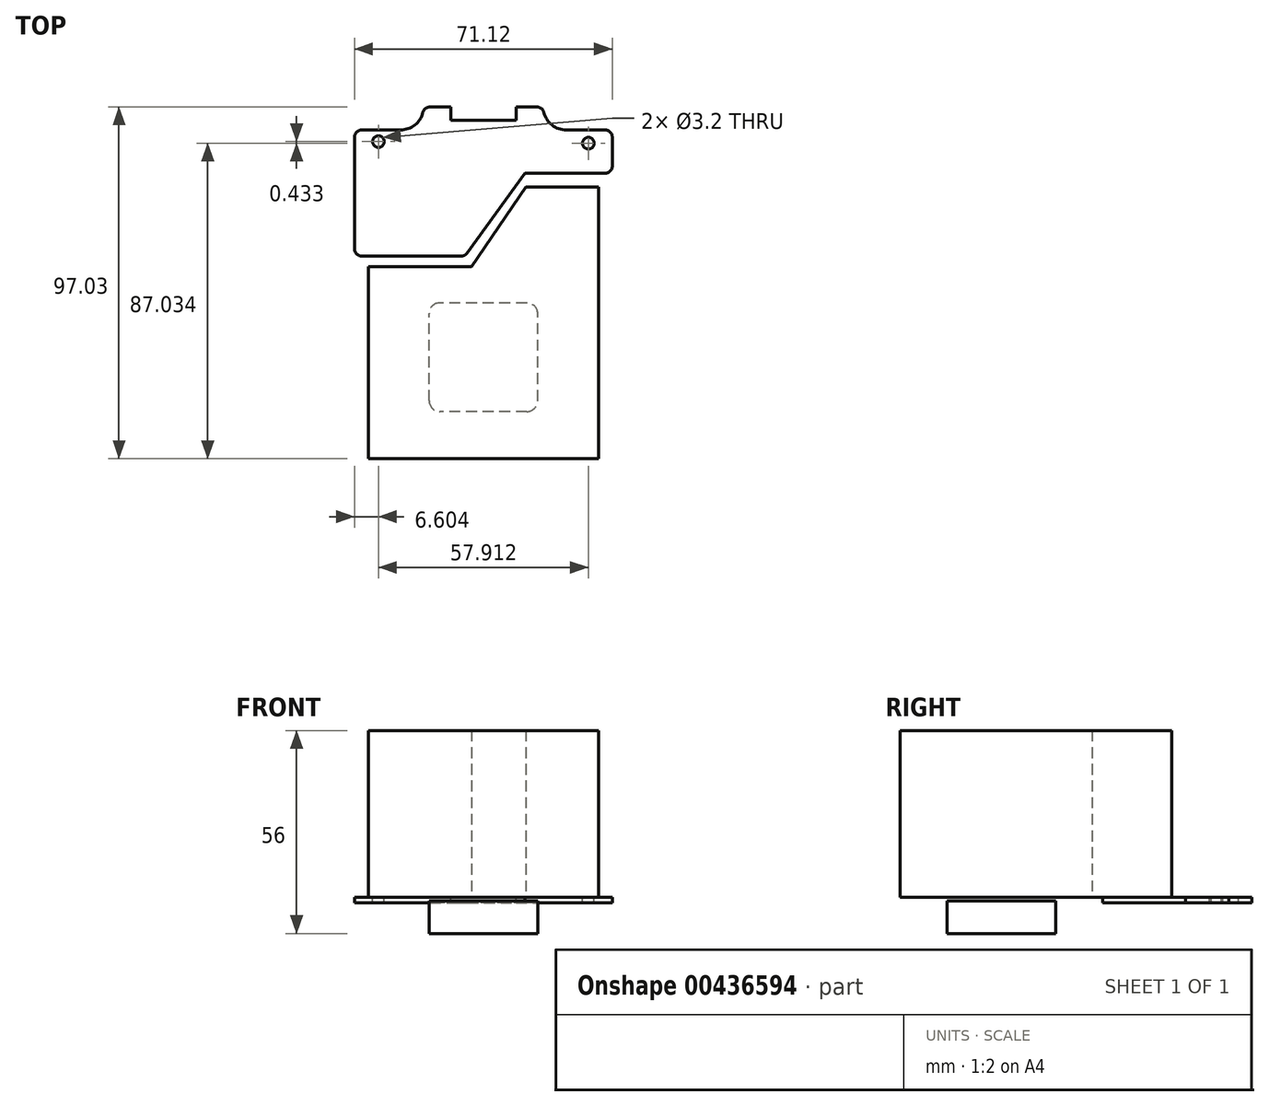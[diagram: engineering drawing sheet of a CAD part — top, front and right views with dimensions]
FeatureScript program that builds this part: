
annotation { "Feature Type Name" : "Feature", "Feature Type Description" : "" }
export const myFeature = defineFeature(function(context is Context, id is Id, definition is map)
    precondition{}
    {
        {
            var Q0;
            Q0=qCreatedBy(makeId("Top.planeOp"),FACE);
            var sketch = newSketch(context, id + "F0", { "sketchPlane" : qUnion([Q0])});
            skLineSegment(sketch, "E0.bottom", {"start": v(35.56, -55.5) * mm, "end": v(-35.56, -55.5) * mm});
            skLineSegment(sketch, "E0.top", {"start": v(35.56, 55.5) * mm, "end": v(-35.56, 55.5) * mm});
            skLineSegment(sketch, "E0.left", {"start": v(35.56, -55.5) * mm, "end": v(35.56, 55.5) * mm});
            skLineSegment(sketch, "E0.right", {"start": v(-35.56, -55.5) * mm, "end": v(-35.56, 55.5) * mm});
            skPoint(sketch, "E0.middle", {"position": v(0, 0) * mm});
            skCircle(sketch, "E1", {"center": v(-28.96, 42.13) * mm, "radius": 1.6 * mm});
            skCircle(sketch, "E2", {"center": v(28.96, 41.7) * mm, "radius": 1.6 * mm});
            skLineSegment(sketch, "E3", {"start": v(-75.95, 0) * mm, "end": v(69.97, 0) * mm, "construction": true});
            skLineSegment(sketch, "E4", {"start": v(0, -74.25) * mm, "end": v(0, 72.53) * mm, "construction": true});
            skLineSegment(sketch, "E5", {"start": v(-28.96, 42.13) * mm, "end": v(28.96, 41.7) * mm, "construction": true});
            skPoint(sketch, "E6", {"position": v(0, 41.91) * mm});
            skCircle(sketch, "E7.MirrorC", {"center": v(-28.96, -42.13) * mm, "radius": 1.6 * mm});
            skCircle(sketch, "E8.MirrorC", {"center": v(28.96, -41.7) * mm, "radius": 1.6 * mm});
            skLineSegment(sketch, "E9.bottom", {"start": v(35.56, 55.5) * mm, "end": v(16.5, 55.5) * mm});
            skLineSegment(sketch, "E9.top", {"start": v(35.56, 45.34) * mm, "end": v(22.86, 45.34) * mm});
            skLineSegment(sketch, "E9.left", {"start": v(35.56, 55.5) * mm, "end": v(35.56, 45.34) * mm});
            skLineSegment(sketch, "E9.right", {"start": v(16.5, 55.5) * mm, "end": v(16.5, 51.69) * mm});
            skPoint(sketch, "E10.visualSharp", {"position": v(16.5, 45.34) * mm});
            skArc(sketch, "E10.filletArc", {"start": v(16.5, 51.69) * mm, "mid": v(18.37, 47.2) * mm, "end": v(22.86, 45.34) * mm});
            skLineSegment(sketch, "E11.MirrorCS", {"start": v(-35.56, 45.34) * mm, "end": v(-22.86, 45.34) * mm});
            skPoint(sketch, "E12.MirrorP", {"position": v(-16.5, 45.34) * mm});
            skArc(sketch, "E13.MirrorCS", {"start": v(-16.5, 51.69) * mm, "mid": v(-18.37, 47.2) * mm, "end": v(-22.86, 45.34) * mm});
            skLineSegment(sketch, "E14.MirrorCS", {"start": v(-16.5, 55.5) * mm, "end": v(-16.5, 51.69) * mm});
            skLineSegment(sketch, "E15.MirrorCS", {"start": v(35.56, -45.34) * mm, "end": v(22.86, -45.34) * mm});
            skArc(sketch, "E16.MirrorCS", {"start": v(16.5, -51.69) * mm, "mid": v(18.37, -47.2) * mm, "end": v(22.86, -45.34) * mm});
            skLineSegment(sketch, "E17.MirrorCS", {"start": v(16.5, -55.5) * mm, "end": v(16.5, -51.69) * mm});
            skLineSegment(sketch, "E18.MirrorCS", {"start": v(-16.5, -55.5) * mm, "end": v(-16.5, -51.69) * mm});
            skArc(sketch, "E19.MirrorCS", {"start": v(-16.5, -51.69) * mm, "mid": v(-18.37, -47.2) * mm, "end": v(-22.86, -45.34) * mm});
            skLineSegment(sketch, "E20.MirrorCS", {"start": v(-35.56, -45.34) * mm, "end": v(-22.86, -45.34) * mm});
            skLineSegment(sketch, "E21", {"start": v(28.96, 41.7) * mm, "end": v(28.96, -41.7) * mm, "construction": true});
            skPoint(sketch, "E22", {"position": v(28.96, 0) * mm});
            skLineSegment(sketch, "E23", {"start": v(-16.5, 51.69) * mm, "end": v(16.5, 51.69) * mm});
            skLineSegment(sketch, "E24", {"start": v(35.56, 33.4) * mm, "end": v(11.44, 33.4) * mm});
            skLineSegment(sketch, "E25", {"start": v(11.44, 33.4) * mm, "end": v(-5.08, 10.54) * mm});
            skLineSegment(sketch, "E26", {"start": v(-5.08, 10.54) * mm, "end": v(-35.56, 10.54) * mm});
            skLineSegment(sketch, "E27.bottom", {"start": v(-9, 55.5) * mm, "end": v(9, 55.5) * mm});
            skLineSegment(sketch, "E27.top", {"start": v(-9, 48) * mm, "end": v(9, 48) * mm});
            skLineSegment(sketch, "E27.left", {"start": v(-9, 55.5) * mm, "end": v(-9, 48) * mm});
            skLineSegment(sketch, "E27.right", {"start": v(9, 55.5) * mm, "end": v(9, 48) * mm});
            skPoint(sketch, "E28", {"position": v(0, 55.5) * mm});
            skSolve(sketch);
        }
        {
            var Q0;
            Q0=qCreatedBy(makeId("Top.planeOp"),FACE);
            var sketch = newSketch(context, id + "F1", { "sketchPlane" : qUnion([Q0])});
            skLineSegment(sketch, "E29.bottom", {"start": v(-31.75, -45.34) * mm, "end": v(31.75, -45.34) * mm});
            skLineSegment(sketch, "E29.top", {"start": v(-31.75, 29.66) * mm, "end": v(31.75, 29.66) * mm});
            skLineSegment(sketch, "E29.left", {"start": v(-31.75, -45.34) * mm, "end": v(-31.75, 29.66) * mm});
            skLineSegment(sketch, "E29.right", {"start": v(31.75, -45.34) * mm, "end": v(31.75, 29.66) * mm});
            skPoint(sketch, "E30", {"position": v(0, 29.66) * mm});
            skLineSegment(sketch, "E31", {"start": v(11.75, 29.66) * mm, "end": v(-3.25, 7.66) * mm});
            skLineSegment(sketch, "E32", {"start": v(-3.25, 7.66) * mm, "end": v(-31.75, 7.66) * mm});
            skLineSegment(sketch, "E33.bottom", {"start": v(12, -32.34) * mm, "end": v(-12, -32.34) * mm});
            skLineSegment(sketch, "E33.top", {"start": v(12, -2.34) * mm, "end": v(-12, -2.34) * mm});
            skLineSegment(sketch, "E33.left", {"start": v(15, -29.34) * mm, "end": v(15, -5.34) * mm});
            skLineSegment(sketch, "E33.right", {"start": v(-15, -29.34) * mm, "end": v(-15, -5.34) * mm});
            skPoint(sketch, "E33.middle", {"position": v(0, -17.34) * mm});
            skPoint(sketch, "E34.visualSharp", {"position": v(15, -2.34) * mm});
            skArc(sketch, "E34.filletArc", {"start": v(15, -5.34) * mm, "mid": v(14.12, -3.22) * mm, "end": v(12, -2.34) * mm});
            skPoint(sketch, "E35.visualSharp", {"position": v(-15, -2.34) * mm});
            skArc(sketch, "E35.filletArc", {"start": v(-12, -2.34) * mm, "mid": v(-14.12, -3.22) * mm, "end": v(-15, -5.34) * mm});
            skPoint(sketch, "E36.visualSharp", {"position": v(-15, -32.34) * mm});
            skArc(sketch, "E36.filletArc", {"start": v(-15, -29.34) * mm, "mid": v(-14.12, -31.46) * mm, "end": v(-12, -32.34) * mm});
            skPoint(sketch, "E37.visualSharp", {"position": v(15, -32.34) * mm});
            skArc(sketch, "E37.filletArc", {"start": v(12, -32.34) * mm, "mid": v(14.12, -31.46) * mm, "end": v(15, -29.34) * mm});
            skSolve(sketch);
        }
        {
            var Q0;
            Q0=makeQuery(id+"F0.imprint","IMPRINT",FACE,{"disambiguationData":[TD([[makeQuery(id+"F0.imprint","IMPRINT",EDGE,{"derivedFrom":sQuery(id+"F0.wireOp",EDGE,"E1")}),-1.0]])]});
            extrude(context, id + "F2", {"entities" : qUnion([Q0]), "depth" : -1.6 * mm});
        }
        {
            var Q0;
            Q0=makeQuery(id+"F1.imprint","IMPRINT",FACE,{"disambiguationData":[TD([[makeQuery(id+"F1.imprint","IMPRINT",EDGE,{"derivedFrom":sQuery(id+"F1.wireOp",EDGE,"E33.bottom")}),-1.0]])]});
            extrude(context, id + "F3", {"entities" : qUnion([Q0]), "operationType" : NewBodyOperationType.REMOVE, "oppositeDirection" : true, "depth" : 19.05 * mm});
        }
        {
            var Q0;
            {var subQ2=sQuery(id+"F1.wireOp",EDGE,"E29.bottom");Q0=makeQuery(id+"F1.imprint","IMPRINT",FACE,{"disambiguationData":[TD([[makeQuery(id+"F1.imprint","IMPRINT",EDGE,{"derivedFrom":subQ2}),1.0]])]});}
            var Q1;
            Q1=makeQuery(id+"F1.imprint","IMPRINT",FACE,{"disambiguationData":[TD([[makeQuery(id+"F1.imprint","IMPRINT",EDGE,{"derivedFrom":sQuery(id+"F1.wireOp",EDGE,"E33.bottom")}),-1.0]])]});
            extrude(context, id + "F4", {"entities" : qUnion([Q0, Q1]), "depth" : 46 * mm});
        }
        {
            var Q0;
            Q0=makeQuery(id+"F1.imprint","IMPRINT",FACE,{"disambiguationData":[TD([[makeQuery(id+"F1.imprint","IMPRINT",EDGE,{"derivedFrom":sQuery(id+"F1.wireOp",EDGE,"E33.bottom")}),-1.0]])]});
            extrude(context, id + "F5", {"entities" : qUnion([Q0]), "operationType" : NewBodyOperationType.ADD, "oppositeDirection" : true, "depth" : 10 * mm});
        }
        {
            var Q0;
            {var subQ2=sQuery(id+"F1.wireOp",EDGE,"E29.bottom");Q0=makeQuery(id+"F1.imprint","IMPRINT",FACE,{"disambiguationData":[TD([[makeQuery(id+"F1.imprint","IMPRINT",EDGE,{"derivedFrom":subQ2}),1.0]])]});}
            var Q1;
            Q1=makeQuery(id+"F1.imprint","IMPRINT",FACE,{"disambiguationData":[TD([[makeQuery(id+"F1.imprint","IMPRINT",EDGE,{"derivedFrom":sQuery(id+"F1.wireOp",EDGE,"E33.bottom")}),-1.0]])]});
            extrude(context, id + "F6", {"entities" : qUnion([Q0, Q1]), "operationType" : NewBodyOperationType.REMOVE, "oppositeDirection" : true, "depth" : 1.02 * mm});
        }
        {
            var Q0;
            Q0=makeQuery(id+"F2.opExtrude","SWEPT_EDGE",EDGE,{"disambiguationData":[OSD([sQuery(id+"F0.wireOp",EDGE,"E13.MirrorCS"),sQuery(id+"F0.wireOp",EDGE,"E14.MirrorCS"),sQuery(id+"F0.wireOp",EDGE,"E23")])]});
            var Q1;
            Q1=makeQuery(id+"F2.opExtrude","SWEPT_EDGE",EDGE,{"disambiguationData":[OSD([sQuery(id+"F0.wireOp",EDGE,"E0.right"),sQuery(id+"F0.wireOp",EDGE,"E11.MirrorCS")])]});
            var Q2;
            Q2=makeQuery(id+"F2.opExtrude","SWEPT_EDGE",EDGE,{"disambiguationData":[OSD([sQuery(id+"F0.wireOp",EDGE,"E0.right"),sQuery(id+"F0.wireOp",EDGE,"E26")])]});
            var Q3;
            Q3=makeQuery(id+"F2.opExtrude","SWEPT_EDGE",EDGE,{"disambiguationData":[OSD([sQuery(id+"F0.wireOp",EDGE,"E25"),sQuery(id+"F0.wireOp",EDGE,"E26")])]});
            var Q4;
            Q4=makeQuery(id+"F2.opExtrude","SWEPT_EDGE",EDGE,{"disambiguationData":[OSD([sQuery(id+"F0.wireOp",EDGE,"E0.left"),sQuery(id+"F0.wireOp",EDGE,"E24")])]});
            var Q5;
            Q5=makeQuery(id+"F2.opExtrude","SWEPT_EDGE",EDGE,{"disambiguationData":[OSD([sQuery(id+"F0.wireOp",EDGE,"E9.right"),sQuery(id+"F0.wireOp",EDGE,"E10.filletArc"),sQuery(id+"F0.wireOp",EDGE,"E23")])]});
            var Q6;
            Q6=makeQuery(id+"F2.opExtrude","SWEPT_EDGE",EDGE,{"disambiguationData":[OSD([sQuery(id+"F0.wireOp",EDGE,"E0.left"),sQuery(id+"F0.wireOp",EDGE,"E9.top"),sQuery(id+"F0.wireOp",EDGE,"E9.left")])]});
            fillet(context, id + "F7", {"entities" : qUnion([Q0, Q1, Q2, Q3, Q4, Q5, Q6]), "radius" : 2 * mm, "tangentPropagation" : true, "allowEdgeOverflow" : false});
        }
    });
